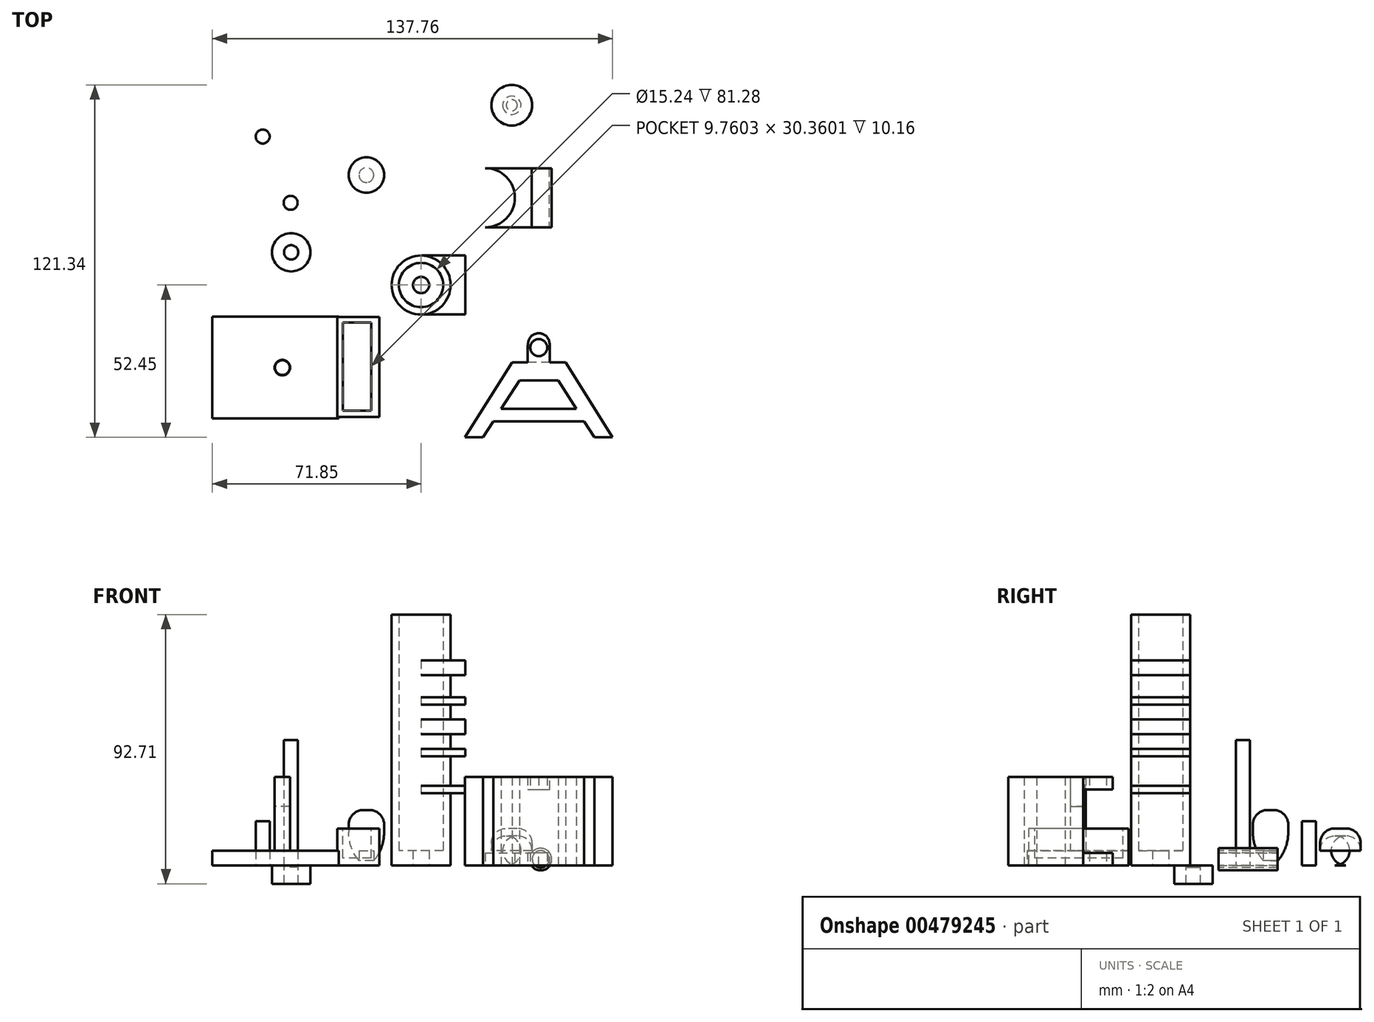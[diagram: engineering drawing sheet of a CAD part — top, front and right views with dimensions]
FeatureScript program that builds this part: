
annotation { "Feature Type Name" : "Feature", "Feature Type Description" : "" }
export const myFeature = defineFeature(function(context is Context, id is Id, definition is map)
    precondition{}
    {
        {
            var Q0;
            Q0=qCreatedBy(makeId("Top.planeOp"),FACE);
            var sketch = newSketch(context, id + "F0", { "sketchPlane" : qUnion([Q0])});
            skCircle(sketch, "E0", {"center": v(0, 0) * mm, "radius": 10.16 * mm});
            skCircle(sketch, "E1", {"center": v(0, 0) * mm, "radius": 7.62 * mm});
            skCircle(sketch, "E2", {"center": v(0, 0) * mm, "radius": 2.8 * mm});
            skSolve(sketch);
        }
        {
            var Q0;
            Q0=makeQuery(id+"F0.imprint","IMPRINT",FACE,{"disambiguationData":[TD([[makeQuery(id+"F0.imprint","IMPRINT",EDGE,{"derivedFrom":sQuery(id+"F0.wireOp",EDGE,"E0")}),1.0]])]});
            extrude(context, id + "F1", {"entities" : qUnion([Q0]), "offsetDistance" : 25.4 * mm, "depth" : 86.36 * mm});
        }
        {
            var Q0;
            Q0=makeQuery(id+"F1.opExtrude","CAP_FACE",FACE,{"disambiguationData":[OSD([sQuery(id+"F0.wireOp",EDGE,"E0")])],"isStart":false});
            var sketch = newSketch(context, id + "F2", { "sketchPlane" : qUnion([Q0])});
            skCircle(sketch, "E3", {"center": v(0, 0) * mm, "radius": 7.62 * mm});
            skSolve(sketch);
        }
        {
            var Q0;
            Q0=makeQuery(id+"F1.opExtrude","CAP_FACE",FACE,{"disambiguationData":[OSD([sQuery(id+"F0.wireOp",EDGE,"E0")])],"isStart":true});
            var sketch = newSketch(context, id + "F3", { "sketchPlane" : qUnion([Q0])});
            skCircle(sketch, "E4", {"center": v(0, 0) * mm, "radius": 2.8 * mm});
            skSolve(sketch);
        }
        {
            var Q0;
            Q0 = qSketchRegion(id + "F3", true);
            extrude(context, id + "F4", {"entities" : qUnion([Q0]), "operationType" : NewBodyOperationType.REMOVE, "oppositeDirection" : true, "offsetDistance" : 25.4 * mm, "depth" : 7.62 * mm});
        }
        {
            var Q0;
            Q0=qCreatedBy(makeId("Top.planeOp"),FACE);
            var sketch = newSketch(context, id + "F5", { "sketchPlane" : qUnion([Q0])});
            skCircle(sketch, "E5", {"center": v(-54.53, 51.13) * mm, "radius": 2.41 * mm});
            skSolve(sketch);
        }
        {
            var Q0;
            Q0=makeQuery(id+"F5.imprint","IMPRINT",FACE,{"disambiguationData":[TD([[makeQuery(id+"F5.imprint","IMPRINT",EDGE,{"derivedFrom":sQuery(id+"F5.wireOp",EDGE,"E5")}),1.0]])]});
            var Q1;
            Q1=sQuery(id+"F5.wireOp",EDGE,"E5");
            extrude(context, id + "F6", {"entities" : qUnion([Q0]), "surfaceEntities" : qUnion([Q1]), "offsetDistance" : 25.4 * mm, "depth" : 15.24 * mm});
        }
        {
            var Q0;
            Q0=qCreatedBy(makeId("Top.planeOp"),FACE);
            var sketch = newSketch(context, id + "F7", { "sketchPlane" : qUnion([Q0])});
            skLineSegment(sketch, "E6.bottom", {"start": v(-15.24, -10.89) * mm, "end": v(-71.85, -10.89) * mm});
            skLineSegment(sketch, "E6.top", {"start": v(-15.24, -46) * mm, "end": v(-71.85, -46) * mm});
            skLineSegment(sketch, "E6.left", {"start": v(-15.24, -10.89) * mm, "end": v(-15.24, -46) * mm});
            skLineSegment(sketch, "E6.right", {"start": v(-71.85, -10.89) * mm, "end": v(-71.85, -46) * mm});
            skLineSegment(sketch, "E7", {"start": v(-28.3, -10.89) * mm, "end": v(-28.3, -46) * mm});
            skSolve(sketch);
        }
        {
            var Q0;
            {var subQ0=sQuery(id+"F7.wireOp",EDGE,"E6.right");Q0=makeQuery(id+"F7.imprint","IMPRINT",FACE,{"disambiguationData":[TD([[makeQuery(id+"F7.imprint","IMPRINT",EDGE,{"derivedFrom":subQ0}),1.0]])]});}
            extrude(context, id + "F8", {"entities" : qUnion([Q0]), "offsetDistance" : 25.4 * mm, "depth" : 5.08 * mm});
        }
        {
            var Q0;
            Q0=qCreatedBy(makeId("Top.planeOp"),FACE);
            var sketch = newSketch(context, id + "F9", { "sketchPlane" : qUnion([Q0])});
            skLineSegment(sketch, "E8.bottom", {"start": v(-28.81, -11) * mm, "end": v(-14.4, -11) * mm});
            skLineSegment(sketch, "E8.top", {"start": v(-28.81, -45.49) * mm, "end": v(-14.4, -45.49) * mm});
            skLineSegment(sketch, "E8.left", {"start": v(-28.81, -11) * mm, "end": v(-28.81, -45.49) * mm});
            skLineSegment(sketch, "E8.right", {"start": v(-14.4, -11) * mm, "end": v(-14.4, -45.49) * mm});
            skSolve(sketch);
        }
        {
            var Q0;
            Q0 = qSketchRegion(id + "F9", true);
            extrude(context, id + "F10", {"entities" : qUnion([Q0]), "operationType" : NewBodyOperationType.ADD, "offsetDistance" : 25.4 * mm, "depth" : 12.7 * mm});
        }
        {
            var Q0;
            Q0=makeQuery(id+"F8.opExtrude","CAP_FACE",FACE,{"disambiguationData":[OSD([sQuery(id+"F7.wireOp",EDGE,"E6.bottom"),sQuery(id+"F7.wireOp",EDGE,"E6.top"),sQuery(id+"F7.wireOp",EDGE,"E6.right"),sQuery(id+"F7.wireOp",EDGE,"E7")])],"isStart":false});
            var sketch = newSketch(context, id + "F11", { "sketchPlane" : qUnion([Q0])});
            skCircle(sketch, "E9", {"center": v(-47.76, -28.44) * mm, "radius": 2.67 * mm});
            skSolve(sketch);
        }
        {
            var Q0;
            Q0 = qSketchRegion(id + "F11", true);
            extrude(context, id + "F12", {"entities" : qUnion([Q0]), "operationType" : NewBodyOperationType.ADD, "offsetDistance" : 25.4 * mm, "depth" : 25.4 * mm});
        }
        {
            var Q0;
            Q0=makeQuery(id+"F12.opExtrude","CAP_FACE",FACE,{"disambiguationData":[OSD([sQuery(id+"F11.wireOp",EDGE,"E9")])],"isStart":false});
            var sketch = newSketch(context, id + "F13", { "sketchPlane" : qUnion([Q0])});
            skCircle(sketch, "E10", {"center": v(-47.76, -28.44) * mm, "radius": 2.54 * mm});
            skSolve(sketch);
        }
        {
            var Q0;
            Q0 = qSketchRegion(id + "F13", true);
            extrude(context, id + "F14", {"entities" : qUnion([Q0]), "operationType" : NewBodyOperationType.REMOVE, "flatOperationType" : FlatOperationType.REMOVE, "oppositeDirection" : true, "offsetDistance" : 25.4 * mm, "depth" : 10.16 * mm, "domain" : OperationDomain.MODEL});
        }
        {
            var Q0;
            Q0=makeQuery(id+"F10.opExtrude","CAP_FACE",FACE,{"disambiguationData":[OSD([sQuery(id+"F9.wireOp",EDGE,"E8.bottom"),sQuery(id+"F9.wireOp",EDGE,"E8.top"),sQuery(id+"F9.wireOp",EDGE,"E8.left"),sQuery(id+"F9.wireOp",EDGE,"E8.right")])],"isStart":false});
            var sketch = newSketch(context, id + "F15", { "sketchPlane" : qUnion([Q0])});
            skLineSegment(sketch, "E11.bottom", {"start": v(-17.18, -12.89) * mm, "end": v(-26.94, -12.89) * mm});
            skLineSegment(sketch, "E11.top", {"start": v(-17.18, -43.25) * mm, "end": v(-26.94, -43.25) * mm});
            skLineSegment(sketch, "E11.left", {"start": v(-17.18, -12.89) * mm, "end": v(-17.18, -43.25) * mm});
            skLineSegment(sketch, "E11.right", {"start": v(-26.94, -12.89) * mm, "end": v(-26.94, -43.25) * mm});
            skSolve(sketch);
        }
        {
            var Q0;
            Q0=makeQuery(id+"F15.imprint","IMPRINT",FACE,{"disambiguationData":[TD([[makeQuery(id+"F15.imprint","IMPRINT",EDGE,{"derivedFrom":sQuery(id+"F15.wireOp",EDGE,"E11.bottom")}),1.0]])]});
            extrude(context, id + "F16", {"entities" : qUnion([Q0]), "operationType" : NewBodyOperationType.REMOVE, "oppositeDirection" : true, "offsetDistance" : 25.4 * mm, "depth" : 10.16 * mm});
        }
        {
            var Q0;
            Q0=qCreatedBy(makeId("Top.planeOp"),FACE);
            var sketch = newSketch(context, id + "F17", { "sketchPlane" : qUnion([Q0])});
            skCircle(sketch, "E12", {"center": v(-44.9, 28.3) * mm, "radius": 2.41 * mm});
            skSolve(sketch);
        }
        {
            var Q0;
            Q0=makeQuery(id+"F17.imprint","IMPRINT",FACE,{"disambiguationData":[TD([[makeQuery(id+"F17.imprint","IMPRINT",EDGE,{"derivedFrom":sQuery(id+"F17.wireOp",EDGE,"E12")}),1.0]])]});
            extrude(context, id + "F18", {"entities" : qUnion([Q0]), "offsetDistance" : 25.4 * mm, "depth" : 43.18 * mm});
        }
        {
            var Q0;
            Q0=qCreatedBy(makeId("Top.planeOp"),FACE);
            var sketch = newSketch(context, id + "F19", { "sketchPlane" : qUnion([Q0])});
            skCircle(sketch, "E13", {"center": v(-20.68, 16.6) * mm, "radius": 6.9 * mm});
            skSolve(sketch);
        }
        {
            var Q0;
            Q0 = qSketchRegion(id + "F19", true);
            extrude(context, id + "F20", {"entities" : qUnion([Q0]), "offsetDistance" : 25.4 * mm, "depth" : 5.08 * mm});
        }
        {
            var Q0;
            Q0=makeQuery(id+"F20.opExtrude","CAP_FACE",FACE,{"disambiguationData":[OSD([sQuery(id+"F19.wireOp",EDGE,"E13")])],"isStart":false});
            var sketch = newSketch(context, id + "F21", { "sketchPlane" : qUnion([Q0])});
            skCircle(sketch, "E14", {"center": v(-20.68, 16.6) * mm, "radius": 2.54 * mm});
            skSolve(sketch);
        }
        {
            var Q0;
            Q0=makeQuery(id+"F21.imprint","IMPRINT",FACE,{"disambiguationData":[TD([[makeQuery(id+"F21.imprint","IMPRINT",EDGE,{"derivedFrom":sQuery(id+"F21.wireOp",EDGE,"E14")}),1.0]])]});
            extrude(context, id + "F22", {"entities" : qUnion([Q0]), "operationType" : NewBodyOperationType.REMOVE, "oppositeDirection" : true, "offsetDistance" : 25.4 * mm, "depth" : 3.8 * mm});
        }
        {
            var Q0;
            Q0=qCreatedBy(makeId("Top.planeOp"),FACE);
            var sketch = newSketch(context, id + "F23", { "sketchPlane" : qUnion([Q0])});
            skCircle(sketch, "E15", {"center": v(-18.83, 37.86) * mm, "radius": 6.1 * mm});
            skSolve(sketch);
        }
        {
            var Q0;
            Q0=makeQuery(id+"F23.imprint","IMPRINT",FACE,{"disambiguationData":[TD([[makeQuery(id+"F23.imprint","IMPRINT",EDGE,{"derivedFrom":sQuery(id+"F23.wireOp",EDGE,"E15")}),1.0]])]});
            extrude(context, id + "F24", {"entities" : qUnion([Q0]), "offsetDistance" : 25.4 * mm, "depth" : 19.05 * mm});
        }
        {
            var Q0;
            Q0=makeQuery(id+"F24.opExtrude","CAP_FACE",FACE,{"disambiguationData":[OSD([sQuery(id+"F23.wireOp",EDGE,"E15")])],"isStart":false});
            fillet(context, id + "F25", {"entities" : qUnion([Q0]), "radius" : 5.08 * mm, "tangentPropagation" : true, "allowEdgeOverflow" : false});
        }
        {
            var Q0;
            Q0=makeQuery(id+"F24.opExtrude","CAP_EDGE",EDGE,{"disambiguationData":[OSD([sQuery(id+"F23.wireOp",EDGE,"E15")])],"isStart":true});
            chamfer(context, id + "F26", {"entities" : qUnion([Q0]), "width" : 5.08 * mm, "tangentPropagation" : true});
        }
        {
            var Q0;
            Q0=makeQuery(id+"F24.opExtrude","SWEPT_FACE",FACE,{"disambiguationData":[OSD([sQuery(id+"F23.wireOp",EDGE,"E15")])]});
            fillet(context, id + "F27", {"entities" : qUnion([Q0]), "radius" : 15.24 * mm, "tangentPropagation" : true, "allowEdgeOverflow" : false});
        }
        {
            var Q0;
            Q0=makeQuery(id+"F24.opExtrude","CAP_FACE",FACE,{"disambiguationData":[OSD([sQuery(id+"F23.wireOp",EDGE,"E15")])],"isStart":true});
            var sketch = newSketch(context, id + "F28", { "sketchPlane" : qUnion([Q0])});
            skCircle(sketch, "E16", {"center": v(-18.83, -37.86) * mm, "radius": 2.54 * mm});
            skSolve(sketch);
        }
        {
            var Q0;
            Q0=makeQuery(id+"F28.imprint","IMPRINT",FACE,{"disambiguationData":[TD([[makeQuery(id+"F28.imprint","IMPRINT",EDGE,{"derivedFrom":sQuery(id+"F28.wireOp",EDGE,"E16")}),1.0]])]});
            extrude(context, id + "F29", {"entities" : qUnion([Q0]), "operationType" : NewBodyOperationType.REMOVE, "oppositeDirection" : true, "offsetDistance" : 25.4 * mm, "depth" : 5.08 * mm});
        }
        {
            var Q0;
            Q0=makeQuery(id+"F24.opExtrude","CAP_FACE",FACE,{"disambiguationData":[OSD([sQuery(id+"F23.wireOp",EDGE,"E15")])],"isStart":true});
            extrude(context, id + "F30", {"entities" : qUnion([Q0]), "operationType" : NewBodyOperationType.REMOVE, "oppositeDirection" : true, "offsetDistance" : 25.4 * mm, "depth" : 5.08 * mm});
        }
        {
            var Q0;
            Q0=qCreatedBy(makeId("Top.planeOp"),FACE);
            var sketch = newSketch(context, id + "F31", { "sketchPlane" : qUnion([Q0])});
            skCircle(sketch, "E17", {"center": v(-44.73, 11.27) * mm, "radius": 6.6 * mm});
            skCircle(sketch, "E18", {"center": v(-44.73, 11.27) * mm, "radius": 2.46 * mm});
            skSolve(sketch);
        }
        {
            var Q0;
            Q0=makeQuery(id+"F31.imprint","IMPRINT",FACE,{"disambiguationData":[TD([[makeQuery(id+"F31.imprint","IMPRINT",EDGE,{"derivedFrom":sQuery(id+"F31.wireOp",EDGE,"E17")}),1.0]])]});
            extrude(context, id + "F32", {"entities" : qUnion([Q0]), "oppositeDirection" : true, "offsetDistance" : 25.4 * mm, "depth" : 6.35 * mm});
        }
        {
            var Q0;
            Q0=makeQuery(id+"F20.opExtrude","SWEPT_BODY",BODY,{"disambiguationData":[OSD([sQuery(id+"F19.wireOp",EDGE,"E13")])]});
            deleteBodies(context, id + "F33", {"entities" : qUnion([Q0])});
        }
        {
            var Q0;
            Q0=qCreatedBy(makeId("Right.planeOp"),FACE);
            var sketch = newSketch(context, id + "F34", { "sketchPlane" : qUnion([Q0])});
            skLineSegment(sketch, "E19.bottom", {"start": v(-10.16, 70.6) * mm, "end": v(10.16, 70.6) * mm});
            skLineSegment(sketch, "E19.top", {"start": v(-10.16, 17.7) * mm, "end": v(10.16, 17.7) * mm});
            skLineSegment(sketch, "E19.left", {"start": v(-10.16, 70.6) * mm, "end": v(-10.16, 17.7) * mm});
            skLineSegment(sketch, "E19.right", {"start": v(10.16, 70.6) * mm, "end": v(10.16, 17.7) * mm});
            skLineSegment(sketch, "E20", {"start": v(-10.16, 70.6) * mm, "end": v(-10.16, 62.97) * mm});
            skLineSegment(sketch, "E21", {"start": v(-10.16, 62.97) * mm, "end": v(-10.16, 55.35) * mm});
            skLineSegment(sketch, "E22", {"start": v(-10.16, 55.35) * mm, "end": v(-10.16, 47.73) * mm});
            skLineSegment(sketch, "E23", {"start": v(-10.16, 47.73) * mm, "end": v(-10.16, 40.11) * mm});
            skLineSegment(sketch, "E24", {"start": v(-10.16, 40.11) * mm, "end": v(-10.16, 32.5) * mm});
            skLineSegment(sketch, "E25", {"start": v(-10.16, 32.5) * mm, "end": v(-10.16, 24.87) * mm});
            skLineSegment(sketch, "E26", {"start": v(-10.16, 24.87) * mm, "end": v(10.16, 24.87) * mm});
            skLineSegment(sketch, "E27", {"start": v(-10.16, 32.5) * mm, "end": v(10.16, 32.5) * mm});
            skLineSegment(sketch, "E28", {"start": v(-10.16, 40.11) * mm, "end": v(10.16, 40.11) * mm});
            skLineSegment(sketch, "E29", {"start": v(-10.16, 47.73) * mm, "end": v(10.16, 47.73) * mm});
            skLineSegment(sketch, "E30", {"start": v(-10.16, 55.35) * mm, "end": v(10.16, 55.35) * mm});
            skLineSegment(sketch, "E31", {"start": v(-10.16, 62.97) * mm, "end": v(10.16, 62.97) * mm});
            skLineSegment(sketch, "E32", {"start": v(-10.16, 70.6) * mm, "end": v(-10.16, 68.05) * mm});
            skLineSegment(sketch, "E33", {"start": v(-10.16, 62.97) * mm, "end": v(-10.16, 65.51) * mm});
            skLineSegment(sketch, "E34", {"start": v(-10.16, 65.51) * mm, "end": v(10.16, 65.51) * mm});
            skLineSegment(sketch, "E35", {"start": v(10.16, 65.51) * mm, "end": v(10.16, 62.97) * mm});
            skLineSegment(sketch, "E36", {"start": v(-10.16, 68.05) * mm, "end": v(10.16, 68.05) * mm});
            skLineSegment(sketch, "E37", {"start": v(-10.16, 55.35) * mm, "end": v(-10.16, 57.9) * mm});
            skLineSegment(sketch, "E38", {"start": v(-10.16, 62.97) * mm, "end": v(-10.16, 60.43) * mm});
            skLineSegment(sketch, "E39", {"start": v(-10.16, 60.43) * mm, "end": v(10.16, 60.43) * mm});
            skLineSegment(sketch, "E40", {"start": v(-10.16, 57.9) * mm, "end": v(10.16, 57.9) * mm});
            skLineSegment(sketch, "E41", {"start": v(-10.16, 55.35) * mm, "end": v(-10.16, 52.81) * mm});
            skLineSegment(sketch, "E42", {"start": v(-10.16, 47.73) * mm, "end": v(-10.16, 48.27) * mm});
            skLineSegment(sketch, "E43", {"start": v(-10.16, 47.73) * mm, "end": v(-10.16, 50.27) * mm});
            skLineSegment(sketch, "E44", {"start": v(-10.16, 50.27) * mm, "end": v(10.16, 50.27) * mm});
            skLineSegment(sketch, "E45", {"start": v(-10.16, 52.81) * mm, "end": v(10.16, 52.81) * mm});
            skLineSegment(sketch, "E46", {"start": v(-10.16, 17.7) * mm, "end": v(-10.16, 20.24) * mm});
            skLineSegment(sketch, "E47", {"start": v(-10.16, 20.24) * mm, "end": v(10.16, 20.24) * mm});
            skLineSegment(sketch, "E48", {"start": v(-10.16, 24.87) * mm, "end": v(-10.16, 22.33) * mm});
            skLineSegment(sketch, "E49", {"start": v(-10.16, 22.33) * mm, "end": v(10.16, 22.33) * mm});
            skLineSegment(sketch, "E50", {"start": v(-10.16, 24.87) * mm, "end": v(-10.16, 27.41) * mm});
            skLineSegment(sketch, "E51", {"start": v(-10.16, 27.41) * mm, "end": v(10.16, 27.41) * mm});
            skLineSegment(sketch, "E52", {"start": v(-10.16, 32.5) * mm, "end": v(-10.16, 29.95) * mm});
            skLineSegment(sketch, "E53", {"start": v(-10.16, 29.95) * mm, "end": v(10.16, 29.95) * mm});
            skLineSegment(sketch, "E54", {"start": v(-10.16, 32.5) * mm, "end": v(-10.16, 35.03) * mm});
            skLineSegment(sketch, "E55", {"start": v(-10.16, 35.03) * mm, "end": v(10.16, 35.03) * mm});
            skLineSegment(sketch, "E56", {"start": v(-10.16, 40.11) * mm, "end": v(-10.16, 37.57) * mm});
            skLineSegment(sketch, "E57", {"start": v(-10.16, 37.57) * mm, "end": v(10.16, 37.57) * mm});
            skLineSegment(sketch, "E58", {"start": v(-10.16, 40.11) * mm, "end": v(-10.16, 42.65) * mm});
            skLineSegment(sketch, "E59", {"start": v(-10.16, 42.65) * mm, "end": v(10.16, 42.65) * mm});
            skLineSegment(sketch, "E60", {"start": v(-10.16, 47.73) * mm, "end": v(-10.16, 45.2) * mm});
            skLineSegment(sketch, "E61", {"start": v(-10.16, 45.2) * mm, "end": v(10.16, 45.2) * mm});
            skPoint(sketch, "E62", {"position": v(-10.16, 20.24) * mm});
            skPoint(sketch, "E63", {"position": v(-10.16, 22.33) * mm});
            skPoint(sketch, "E64", {"position": v(-10.16, 24.87) * mm});
            skPoint(sketch, "E65", {"position": v(-10.16, 27.41) * mm});
            skPoint(sketch, "E66", {"position": v(-10.16, 29.95) * mm});
            skPoint(sketch, "E67", {"position": v(-10.16, 32.5) * mm});
            skPoint(sketch, "E68", {"position": v(-10.16, 35.03) * mm});
            skPoint(sketch, "E69", {"position": v(-10.16, 37.57) * mm});
            skPoint(sketch, "E70", {"position": v(-10.16, 40.11) * mm});
            skPoint(sketch, "E71", {"position": v(-10.16, 42.65) * mm});
            skPoint(sketch, "E72", {"position": v(-10.16, 45.2) * mm});
            skPoint(sketch, "E73", {"position": v(-10.16, 47.73) * mm});
            skPoint(sketch, "E74", {"position": v(-10.16, 50.27) * mm});
            skPoint(sketch, "E75", {"position": v(-10.16, 52.81) * mm});
            skPoint(sketch, "E76", {"position": v(-10.16, 55.35) * mm});
            skPoint(sketch, "E77", {"position": v(-10.16, 57.9) * mm});
            skPoint(sketch, "E78", {"position": v(-10.16, 60.43) * mm});
            skPoint(sketch, "E79", {"position": v(-10.16, 62.97) * mm});
            skPoint(sketch, "E80", {"position": v(-10.16, 65.51) * mm});
            skPoint(sketch, "E81", {"position": v(-10.16, 68.05) * mm});
            skPoint(sketch, "E82", {"position": v(-10.16, 70.6) * mm});
            skLineSegment(sketch, "E83", {"start": v(-10.16, 70.6) * mm, "end": v(-10.16, 65.51) * mm});
            skSolve(sketch);
        }
        {
            var Q0;
            {var subQ0=sQuery(id+"F34.wireOp",EDGE,"E19.bottom");Q0=makeQuery(id+"F34.imprint","IMPRINT",FACE,{"disambiguationData":[TD([[makeQuery(id+"F34.imprint","IMPRINT",EDGE,{"derivedFrom":subQ0}),-1.0]])]});}
            var Q1;
            {var subQ0=sQuery(id+"F34.wireOp",EDGE,"E34");Q1=makeQuery(id+"F34.imprint","IMPRINT",FACE,{"disambiguationData":[TD([[makeQuery(id+"F34.imprint","IMPRINT",EDGE,{"derivedFrom":subQ0}),1.0]])]});}
            var Q2;
            Q2=makeQuery(id+"F34.imprint","IMPRINT",FACE,{"disambiguationData":[TD([[makeQuery(id+"F34.imprint","IMPRINT",EDGE,{"derivedFrom":sQuery(id+"F34.wireOp",EDGE,"E21")}),1.0]])]});
            var Q3;
            {var subQ0=sQuery(id+"F34.wireOp",EDGE,"E30");Q3=makeQuery(id+"F34.imprint","IMPRINT",FACE,{"disambiguationData":[TD([[makeQuery(id+"F34.imprint","IMPRINT",EDGE,{"derivedFrom":subQ0}),1.0]])]});}
            var Q4;
            {var subQ0=sQuery(id+"F34.wireOp",EDGE,"E29");Q4=makeQuery(id+"F34.imprint","IMPRINT",FACE,{"disambiguationData":[TD([[makeQuery(id+"F34.imprint","IMPRINT",EDGE,{"derivedFrom":subQ0}),1.0]])]});}
            var Q5;
            {var subQ0=sQuery(id+"F34.wireOp",EDGE,"E29");Q5=makeQuery(id+"F34.imprint","IMPRINT",FACE,{"disambiguationData":[TD([[makeQuery(id+"F34.imprint","IMPRINT",EDGE,{"derivedFrom":subQ0}),-1.0]])]});}
            var Q6;
            {var subQ0=sQuery(id+"F34.wireOp",EDGE,"E28");Q6=makeQuery(id+"F34.imprint","IMPRINT",FACE,{"disambiguationData":[TD([[makeQuery(id+"F34.imprint","IMPRINT",EDGE,{"derivedFrom":subQ0}),-1.0]])]});}
            var Q7;
            Q7=makeQuery(id+"F34.imprint","IMPRINT",FACE,{"disambiguationData":[TD([[makeQuery(id+"F34.imprint","IMPRINT",EDGE,{"derivedFrom":sQuery(id+"F34.wireOp",EDGE,"E24")}),1.0]])]});
            var Q8;
            Q8=makeQuery(id+"F34.imprint","IMPRINT",FACE,{"disambiguationData":[TD([[makeQuery(id+"F34.imprint","IMPRINT",EDGE,{"derivedFrom":sQuery(id+"F34.wireOp",EDGE,"E25")}),1.0]])]});
            var Q9;
            {var subQ0=sQuery(id+"F34.wireOp",EDGE,"E26");Q9=makeQuery(id+"F34.imprint","IMPRINT",FACE,{"disambiguationData":[TD([[makeQuery(id+"F34.imprint","IMPRINT",EDGE,{"derivedFrom":subQ0}),1.0]])]});}
            extrude(context, id + "F35", {"entities" : qUnion([Q0, Q1, Q2, Q3, Q4, Q5, Q6, Q7, Q8, Q9]), "operationType" : NewBodyOperationType.ADD, "flatOperationType" : FlatOperationType.REMOVE, "depth" : 15.24 * mm, "offsetDistance" : 25.4 * mm, "domain" : OperationDomain.MODEL});
        }
        {
            var Q0;
            Q0=makeQuery(id+"F2.imprint","IMPRINT",FACE,{"disambiguationData":[TD([[makeQuery(id+"F2.imprint","IMPRINT",EDGE,{"derivedFrom":sQuery(id+"F2.wireOp",EDGE,"E3")}),1.0]])]});
            extrude(context, id + "F36", {"entities" : qUnion([Q0]), "operationType" : NewBodyOperationType.REMOVE, "oppositeDirection" : true, "depth" : 88.9 * mm, "offsetDistance" : 25.4 * mm});
        }
        {
            var Q0;
            Q0=makeQuery(id+"F31.imprint","IMPRINT",FACE,{"disambiguationData":[TD([[makeQuery(id+"F31.imprint","IMPRINT",EDGE,{"derivedFrom":sQuery(id+"F31.wireOp",EDGE,"E18")}),1.0]])]});
            extrude(context, id + "F37", {"entities" : qUnion([Q0]), "oppositeDirection" : true, "depth" : 0.64 * mm, "offsetDistance" : 25.4 * mm});
        }
        {
            var Q0;
            Q0=makeQuery(id+"F0.imprint","IMPRINT",FACE,{"disambiguationData":[TD([[makeQuery(id+"F0.imprint","IMPRINT",EDGE,{"derivedFrom":sQuery(id+"F0.wireOp",EDGE,"E1")}),1.0]])]});
            extrude(context, id + "F38", {"entities" : qUnion([Q0]), "operationType" : NewBodyOperationType.ADD, "depth" : 5.08 * mm, "offsetDistance" : 25.4 * mm});
        }
        {
            var Q0;
            Q0=qCreatedBy(makeId("Top.planeOp"),FACE);
            var sketch = newSketch(context, id + "F39", { "sketchPlane" : qUnion([Q0])});
            skLineSegment(sketch, "E84.bottom", {"start": v(22.14, 40.22) * mm, "end": v(37.38, 40.22) * mm});
            skLineSegment(sketch, "E84.top", {"start": v(22.14, 19.9) * mm, "end": v(37.38, 19.9) * mm});
            skLineSegment(sketch, "E84.left", {"start": v(22.14, 40.22) * mm, "end": v(22.14, 19.9) * mm});
            skLineSegment(sketch, "E84.right", {"start": v(37.38, 40.22) * mm, "end": v(37.38, 19.9) * mm});
            skLineSegment(sketch, "E85", {"start": v(37.38, 30.06) * mm, "end": v(32.3, 30.06) * mm});
            skArc(sketch, "E86", {"start": v(22.14, 19.9) * mm, "mid": v(32.3, 30.06) * mm, "end": v(22.14, 40.22) * mm});
            skSolve(sketch);
        }
        {
            var Q0;
            {var subQ0=sQuery(id+"F39.wireOp",EDGE,"E84.bottom");Q0=makeQuery(id+"F39.imprint","IMPRINT",FACE,{"disambiguationData":[TD([[makeQuery(id+"F39.imprint","IMPRINT",EDGE,{"derivedFrom":subQ0}),-1.0]])]});}
            var Q1;
            {var subQ0=sQuery(id+"F39.wireOp",EDGE,"E84.top");Q1=makeQuery(id+"F39.imprint","IMPRINT",FACE,{"disambiguationData":[TD([[makeQuery(id+"F39.imprint","IMPRINT",EDGE,{"derivedFrom":subQ0}),1.0]])]});}
            extrude(context, id + "F40", {"entities" : qUnion([Q0, Q1]), "depth" : 4.32 * mm, "offsetDistance" : 25.4 * mm});
        }
        {
            var Q0;
            Q0=makeQuery(id+"F40.opExtrude","SWEPT_FACE",FACE,{"disambiguationData":[OSD([sQuery(id+"F39.wireOp",EDGE,"E84.top")])]});
            var sketch = newSketch(context, id + "F41", { "sketchPlane" : qUnion([Q0])});
            skLineSegment(sketch, "E87", {"start": v(37.38, 2.16) * mm, "end": v(45, 2.16) * mm});
            skCircle(sketch, "E88", {"center": v(41.19, 2.05) * mm, "radius": 3.81 * mm});
            skPoint(sketch, "E88.third.point", {"position": v(40.58, -1.7) * mm});
            skLineSegment(sketch, "E89", {"start": v(37.38, 0) * mm, "end": v(37.98, 0) * mm});
            skLineSegment(sketch, "E90", {"start": v(37.38, 4.32) * mm, "end": v(38.12, 4.32) * mm});
            skCircle(sketch, "E91", {"center": v(41.19, 2.16) * mm, "radius": 2.92 * mm});
            skSolve(sketch);
        }
        {
            var Q0;
            Q0 = qSketchRegion(id + "F41", true);
            var Q1;
            {var subQ0=sQuery(id+"F41.wireOp",EDGE,"SE0pehnD-vHAa-jRD7-sHrf-EHHxooQLke2a");Q1=makeQuery(id+"F41.imprint","IMPRINT",FACE,{"disambiguationData":[TD([[makeQuery(id+"F41.imprint","IMPRINT",EDGE,{"derivedFrom":subQ0}),1.0]])]});}
            var Q2;
            {var subQ4=sQuery(id+"F41.wireOp",EDGE,"nSWaovxP-GCoH-wVAA-aq1m-IAtZV5V13Fk2");Q2=makeQuery(id+"F41.imprint","IMPRINT",FACE,{"disambiguationData":[TD([[makeQuery(id+"F41.imprint","IMPRINT",EDGE,{"derivedFrom":subQ4}),-1.0]])]});}
            var Q3;
            {var subQ0=sQuery(id+"F41.wireOp",EDGE,"E89");Q3=makeQuery(id+"F41.imprint","IMPRINT",FACE,{"disambiguationData":[TD([[makeQuery(id+"F41.imprint","IMPRINT",EDGE,{"derivedFrom":subQ0}),1.0]])]});}
            var Q4;
            {var subQ4=sQuery(id+"F41.wireOp",EDGE,"E90");Q4=makeQuery(id+"F41.imprint","IMPRINT",FACE,{"disambiguationData":[TD([[makeQuery(id+"F41.imprint","IMPRINT",EDGE,{"derivedFrom":subQ4}),-1.0]])]});}
            extrude(context, id + "F42", {"entities" : qUnion([Q0, Q1, Q2, Q3, Q4]), "operationType" : NewBodyOperationType.ADD, "oppositeDirection" : true, "depth" : 20.32 * mm, "offsetDistance" : 25.4 * mm});
        }
        {
            var Q0;
            Q0=qCreatedBy(makeId("Top.planeOp"),FACE);
            var sketch = newSketch(context, id + "F43", { "sketchPlane" : qUnion([Q0])});
            skLineSegment(sketch, "E92", {"start": v(15.11, -52.45) * mm, "end": v(65.91, -52.45) * mm});
            skLineSegment(sketch, "E93", {"start": v(65.91, -52.45) * mm, "end": v(49.72, -26.63) * mm});
            skLineSegment(sketch, "E94", {"start": v(15.11, -52.45) * mm, "end": v(31.32, -52.45) * mm});
            skLineSegment(sketch, "E95", {"start": v(15.11, -52.45) * mm, "end": v(31.32, -26.63) * mm});
            skLineSegment(sketch, "E96", {"start": v(31.32, -26.63) * mm, "end": v(49.72, -26.63) * mm});
            skLineSegment(sketch, "E97", {"start": v(21.34, -52.45) * mm, "end": v(15.11, -52.45) * mm});
            skLineSegment(sketch, "E98", {"start": v(65.91, -52.45) * mm, "end": v(59.69, -52.45) * mm});
            skLineSegment(sketch, "E99", {"start": v(59.69, -52.45) * mm, "end": v(47.2, -32.85) * mm});
            skLineSegment(sketch, "E100", {"start": v(33.84, -32.85) * mm, "end": v(21.34, -52.45) * mm});
            skLineSegment(sketch, "E101", {"start": v(33.84, -32.85) * mm, "end": v(47.2, -32.85) * mm});
            skLineSegment(sketch, "E102", {"start": v(27.59, -42.65) * mm, "end": v(53.44, -42.65) * mm});
            skLineSegment(sketch, "E103", {"start": v(53.44, -42.65) * mm, "end": v(56.17, -46.94) * mm});
            skLineSegment(sketch, "E104", {"start": v(56.17, -46.94) * mm, "end": v(24.85, -46.94) * mm});
            skSolve(sketch);
        }
        {
            var Q0;
            {var subQ0=sQuery(id+"F43.wireOp",EDGE,"E102");Q0=makeQuery(id+"F43.imprint","IMPRINT",FACE,{"disambiguationData":[TD([[makeQuery(id+"F43.imprint","IMPRINT",EDGE,{"derivedFrom":subQ0}),-1.0]])]});}
            var Q1;
            Q1=makeQuery(id+"F43.imprint","IMPRINT",FACE,{"disambiguationData":[TD([[makeQuery(id+"F43.imprint","IMPRINT",EDGE,{"derivedFrom":sQuery(id+"F43.wireOp",EDGE,"E93")}),1.0]])]});
            extrude(context, id + "F44", {"entities" : qUnion([Q0, Q1]), "depth" : 30.48 * mm, "offsetDistance" : 25.4 * mm});
        }
        {
            var Q0;
            Q0=makeQuery(id+"F44.opExtrude","SWEPT_FACE",FACE,{"disambiguationData":[OSD([sQuery(id+"F43.wireOp",EDGE,"E96")])]});
            var sketch = newSketch(context, id + "F45", { "sketchPlane" : qUnion([Q0])});
            skLineSegment(sketch, "E105.bottom", {"start": v(-40.52, 30.48) * mm, "end": v(-44.33, 30.48) * mm});
            skLineSegment(sketch, "E105.top", {"start": v(-40.52, 30.48) * mm, "end": v(-44.33, 30.48) * mm});
            skLineSegment(sketch, "E105.left", {"start": v(-40.52, 30.48) * mm, "end": v(-40.52, 30.48) * mm});
            skLineSegment(sketch, "E105.right", {"start": v(-44.33, 30.48) * mm, "end": v(-44.33, 30.48) * mm});
            skLineSegment(sketch, "E106", {"start": v(-40.52, 30.48) * mm, "end": v(-36.7, 30.48) * mm});
            skLineSegment(sketch, "E107", {"start": v(-36.7, 30.48) * mm, "end": v(-36.7, 26.16) * mm});
            skLineSegment(sketch, "E108", {"start": v(-36.7, 26.16) * mm, "end": v(-44.33, 26.16) * mm});
            skLineSegment(sketch, "E109", {"start": v(-44.33, 26.16) * mm, "end": v(-44.33, 30.48) * mm});
            skLineSegment(sketch, "E110", {"start": v(-44.33, 0) * mm, "end": v(-44.33, 4.32) * mm});
            skLineSegment(sketch, "E111", {"start": v(-44.33, 4.32) * mm, "end": v(-36.7, 4.32) * mm});
            skLineSegment(sketch, "E112", {"start": v(-36.7, 4.32) * mm, "end": v(-36.7, 0) * mm});
            skLineSegment(sketch, "E113", {"start": v(-36.7, 0) * mm, "end": v(-44.33, 0) * mm});
            skSolve(sketch);
        }
        {
            var Q0;
            Q0 = qSketchRegion(id + "F45", true);
            extrude(context, id + "F46", {"entities" : qUnion([Q0]), "operationType" : NewBodyOperationType.ADD, "depth" : 10.16 * mm, "offsetDistance" : 25.4 * mm});
        }
        {
            var Q0;
            Q0=makeQuery(id+"F46.boolean.opBoolean","MERGE",FACE,{"derivedFrom":[makeQuery(id+"F44.opExtrude","CAP_FACE",FACE,{"disambiguationData":[OSD([sQuery(id+"F43.wireOp",EDGE,"E93"),sQuery(id+"F43.wireOp",EDGE,"E95"),sQuery(id+"F43.wireOp",EDGE,"E96"),sQuery(id+"F43.wireOp",EDGE,"E97"),sQuery(id+"F43.wireOp",EDGE,"E98"),sQuery(id+"F43.wireOp",EDGE,"E99"),sQuery(id+"F43.wireOp",EDGE,"E100"),sQuery(id+"F43.wireOp",EDGE,"E101"),sQuery(id+"F43.wireOp",EDGE,"E102"),sQuery(id+"F43.wireOp",EDGE,"E104")])],"isStart":true}),makeQuery(id+"F46.opExtrude","SWEPT_FACE",FACE,{"disambiguationData":[OSD([sQuery(id+"F45.wireOp",EDGE,"E113")])]})]});
            var sketch = newSketch(context, id + "F47", { "sketchPlane" : qUnion([Q0])});
            skLineSegment(sketch, "E114", {"start": v(36.7, 26.63) * mm, "end": v(36.7, 21.55) * mm});
            skLineSegment(sketch, "E115", {"start": v(36.7, 21.55) * mm, "end": v(40.52, 21.55) * mm});
            skCircle(sketch, "E116", {"center": v(40.52, 21.55) * mm, "radius": 2.92 * mm});
            skSolve(sketch);
        }
        {
            var Q0;
            Q0=makeQuery(id+"F47.imprint","IMPRINT",FACE,{"disambiguationData":[TD([[makeQuery(id+"F47.imprint","IMPRINT",EDGE,{"derivedFrom":sQuery(id+"F47.wireOp",EDGE,"E116")}),1.0]])]});
            extrude(context, id + "F48", {"entities" : qUnion([Q0]), "operationType" : NewBodyOperationType.REMOVE, "oppositeDirection" : true, "depth" : 35.56 * mm, "offsetDistance" : 25.4 * mm});
        }
        {
            var Q0;
            Q0=makeQuery(id+"F46.opExtrude","CAP_EDGE",EDGE,{"disambiguationData":[OSD([sQuery(id+"F45.wireOp",EDGE,"E110")])],"isStart":false});
            var Q1;
            Q1=makeQuery(id+"F46.opExtrude","CAP_EDGE",EDGE,{"disambiguationData":[OSD([sQuery(id+"F45.wireOp",EDGE,"E112")])],"isStart":false});
            var Q2;
            Q2=makeQuery(id+"F46.opExtrude","CAP_EDGE",EDGE,{"disambiguationData":[OSD([sQuery(id+"F45.wireOp",EDGE,"E107")])],"isStart":false});
            var Q3;
            Q3=makeQuery(id+"F46.opExtrude","CAP_EDGE",EDGE,{"disambiguationData":[OSD([sQuery(id+"F45.wireOp",EDGE,"E109")])],"isStart":false});
            fillet(context, id + "F49", {"entities" : qUnion([Q0, Q1, Q2, Q3]), "radius" : 5.08 * mm, "tangentPropagation" : true, "rho" : .534, "crossSection" : FilletCrossSection.CONIC, "allowEdgeOverflow" : false});
        }
        {
            var Q0;
            Q0=qCreatedBy(makeId("Top.planeOp"),FACE);
            var sketch = newSketch(context, id + "F50", { "sketchPlane" : qUnion([Q0])});
            skCircle(sketch, "E117", {"center": v(31.23, 61.9) * mm, "radius": 6.99 * mm});
            skSolve(sketch);
        }
        {
            var Q0;
            Q0 = qSketchRegion(id + "F50", true);
            extrude(context, id + "F51", {"entities" : qUnion([Q0]), "depth" : 12.7 * mm, "offsetDistance" : 25.4 * mm});
        }
        {
            var Q0;
            Q0=makeQuery(id+"F51.opExtrude","CAP_FACE",FACE,{"disambiguationData":[OSD([sQuery(id+"F50.wireOp",EDGE,"E117")])],"isStart":false});
            var Q1;
            Q1=makeQuery(id+"F51.opExtrude","SWEPT_FACE",FACE,{"disambiguationData":[OSD([sQuery(id+"F50.wireOp",EDGE,"E117")])]});
            fillet(context, id + "F52", {"entities" : qUnion([Q0, Q1]), "radius" : 5.08 * mm, "tangentPropagation" : true, "allowEdgeOverflow" : false});
        }
    });
